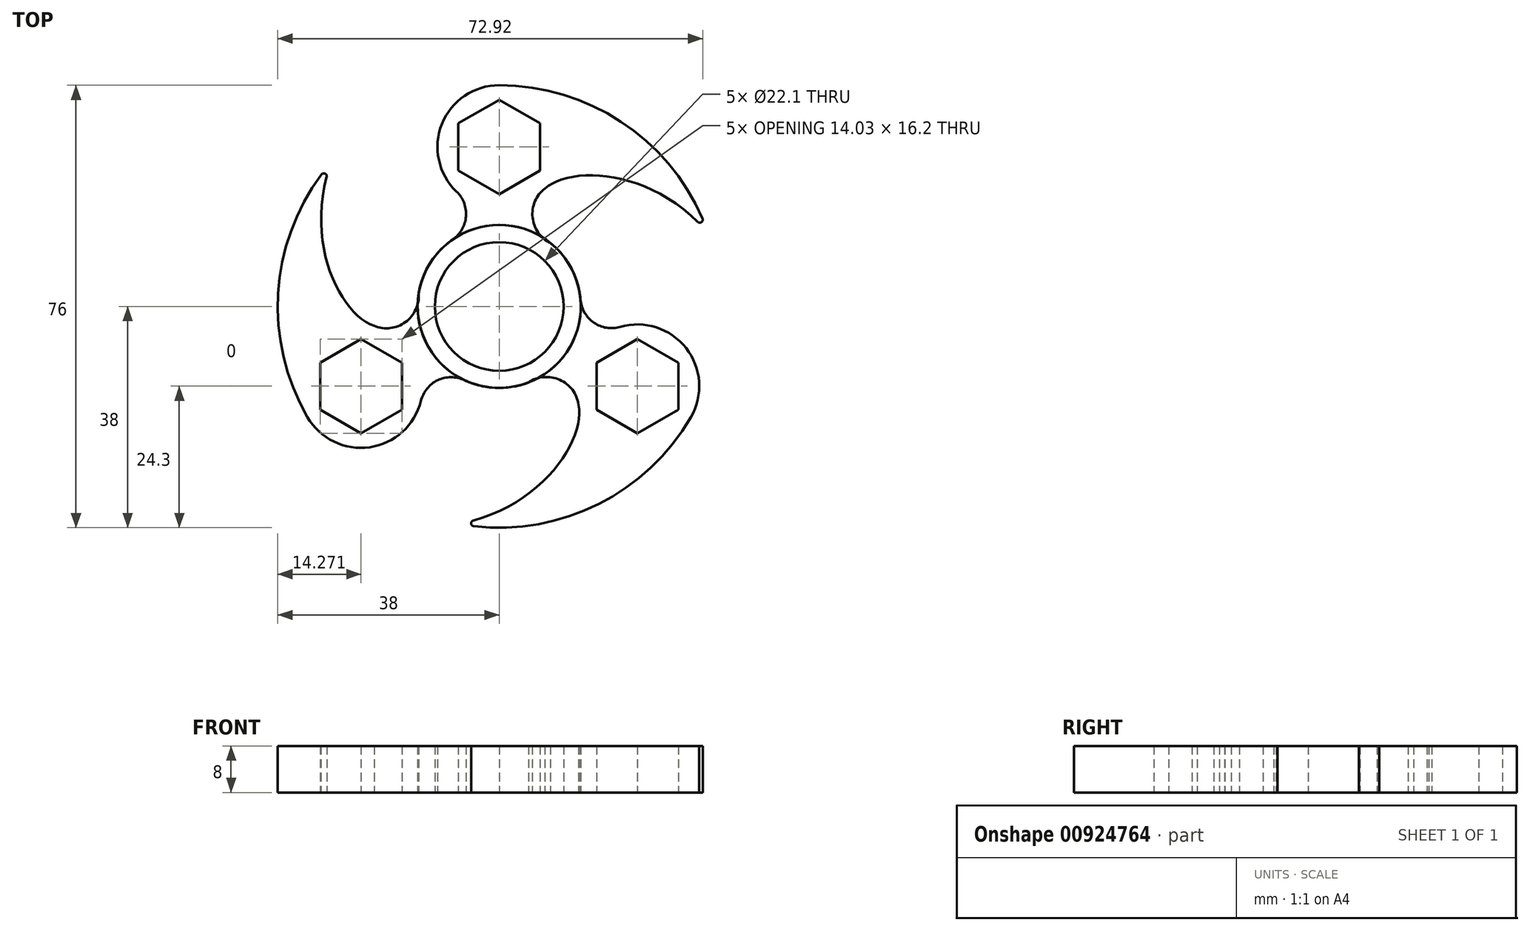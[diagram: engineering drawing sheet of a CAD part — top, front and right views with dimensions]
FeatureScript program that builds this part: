
annotation { "Feature Type Name" : "Feature", "Feature Type Description" : "" }
export const myFeature = defineFeature(function(context is Context, id is Id, definition is map)
    precondition{}
    {
        {
            var Q0;
            Q0=qCreatedBy(makeId("Top.planeOp"),FACE);
            var sketch = newSketch(context, id + "F0", { "sketchPlane" : qUnion([Q0])});
            skCircle(sketch, "E0", {"center": v(0, 0) * mm, "radius": 14 * mm});
            skLineSegment(sketch, "E1", {"start": v(-26.87, 26.87) * mm, "end": v(26.87, -26.87) * mm, "construction": true});
            skLineSegment(sketch, "E2.MirrorCS", {"start": v(26.87, 26.87) * mm, "end": v(-26.87, -26.87) * mm, "construction": true});
            skPoint(sketch, "E3", {"position": v(9.9, -9.9) * mm});
            skPoint(sketch, "E4", {"position": v(-9.9, -9.9) * mm});
            skPoint(sketch, "E5", {"position": v(9.9, 9.9) * mm});
            skPoint(sketch, "E6", {"position": v(-9.9, 9.9) * mm});
            skLineSegment(sketch, "E7", {"start": v(0, 0) * mm, "end": v(-32.9, -19) * mm, "construction": true});
            skLineSegment(sketch, "E8.MirrorCS", {"start": v(0, 0) * mm, "end": v(32.9, -19) * mm, "construction": true});
            skCircle(sketch, "E9.cCircle", {"center": v(23.73, -13.7) * mm, "radius": 7.01 * mm, "construction": true});
            skLineSegment(sketch, "E9.0", {"start": v(16.71, -9.65) * mm, "end": v(23.73, -5.6) * mm});
            skLineSegment(sketch, "E9.1", {"start": v(23.73, -5.6) * mm, "end": v(30.74, -9.65) * mm});
            skLineSegment(sketch, "E9.2", {"start": v(30.74, -9.65) * mm, "end": v(30.74, -17.75) * mm});
            skLineSegment(sketch, "E9.3", {"start": v(30.74, -17.75) * mm, "end": v(23.73, -21.8) * mm});
            skLineSegment(sketch, "E9.4", {"start": v(23.73, -21.8) * mm, "end": v(16.71, -17.75) * mm});
            skLineSegment(sketch, "E9.5", {"start": v(16.71, -17.75) * mm, "end": v(16.71, -9.65) * mm});
            skPoint(sketch, "E9.0.midPoint", {"position": v(20.22, -7.62) * mm});
            skPoint(sketch, "E10", {"position": v(12.12, -7) * mm});
            skPoint(sketch, "E11", {"position": v(12.68, -7.32) * mm});
            skCircle(sketch, "E12", {"center": v(0, 0) * mm, "radius": 38 * mm});
            skCircle(sketch, "E13", {"center": v(23.73, -13.7) * mm, "radius": 10.6 * mm});
            skPoint(sketch, "E14.first.point", {"position": v(13.63, -16.9) * mm});
            skPoint(sketch, "E14.second.point", {"position": v(5.05, -13.06) * mm});
            skPoint(sketch, "E14.third.point", {"position": v(1.3, -17.95) * mm});
            skPoint(sketch, "E15.center", {"position": v(0.94, -0.54) * mm});
            skLineSegment(sketch, "E15.anchor1", {"start": v(0.94, -0.54) * mm, "end": v(23.73, -13.7) * mm, "construction": true});
            skLineSegment(sketch, "E15.anchor2", {"start": v(0.94, -0.54) * mm, "end": v(0.94, 25.78) * mm, "construction": true});
            skFitSpline(sketch, "E16", {"points": [v(13.63, -16.9) * mm, v(-7, -37.35) * mm], "startDerivative": vector(3.53, -17.94) * mm, "endDerivative": vector(-42.9, -7.87) * mm});
            skArc(sketch, "E17", {"start": v(13.63, -16.9) * mm, "mid": v(10.39, -12.6) * mm, "end": v(5.02, -13.07) * mm});
            skArc(sketch, "E18", {"start": v(20.77, -3.52) * mm, "mid": v(16.25, -2.8) * mm, "end": v(13.95, 1.16) * mm});
            skCircle(sketch, "E19", {"center": v(0, 0) * mm, "radius": 11.05 * mm});
            skSolve(sketch);
        }
        {
            var Q0;
            Q0=makeQuery(id+"F0.imprint","IMPRINT",FACE,{"disambiguationData":[TD([[makeQuery(id+"F0.imprint","IMPRINT",EDGE,{"derivedFrom":sQuery(id+"F0.wireOp",EDGE,"E9.0")}),1.0]])]});
            var Q1;
            {var subQ0=sQuery(id+"F0.wireOp",EDGE,"E16");var subQ1=sQuery(id+"F0.wireOp",EDGE,"E12");var subQ2=makeQuery(id+"F0.imprint","INTERSECT",VERTEX,{"derivedFrom":[subQ1,subQ0]});Q1=makeQuery(id+"F0.imprint","IMPRINT",FACE,{"disambiguationData":[TD([[makeQuery(id+"F0.imprint","IMPRINT",EDGE,{"disambiguationData":[TD([[subQ2,-1.0]])],"derivedFrom":subQ1}),1.0]])]});}
            var Q2;
            {var subQ0=sQuery(id+"F0.wireOp",EDGE,"E17");Q2=makeQuery(id+"F0.imprint","IMPRINT",FACE,{"disambiguationData":[TD([[makeQuery(id+"F0.imprint","IMPRINT",EDGE,{"derivedFrom":subQ0}),-1.0]])]});}
            extrude(context, id + "F1", {"entities" : qUnion([Q0, Q1, Q2]), "depth" : 8 * mm, "offsetDistance" : 25 * mm});
        }
        {
            var Q0;
            Q0=qCreatedBy(makeId("Front.planeOp"),FACE);
            var sketch = newSketch(context, id + "F2", { "sketchPlane" : qUnion([Q0])});
            skLineSegment(sketch, "E20", {"start": v(0, 50.96) * mm, "end": v(0, -45.31) * mm, "construction": true});
            skSolve(sketch);
        }
        {
            var Q0;
            Q0=makeQuery(id+"F1.opExtrude","SWEPT_EDGE",EDGE,{"disambiguationData":[OSD([sQuery(id+"F0.wireOp",EDGE,"E12"),sQuery(id+"F0.wireOp",EDGE,"E16")])]});
            fillet(context, id + "F3", {"entities" : qUnion([Q0]), "radius" : .5 * mm, "tangentPropagation" : true, "allowEdgeOverflow" : false});
        }
        {
            var Q0;
            Q0=makeQuery(id+"F1.opExtrude","SWEPT_BODY",BODY,{"disambiguationData":[OSD([sQuery(id+"F0.wireOp",EDGE,"E9.0"),sQuery(id+"F0.wireOp",EDGE,"E9.1"),sQuery(id+"F0.wireOp",EDGE,"E9.2"),sQuery(id+"F0.wireOp",EDGE,"E9.3"),sQuery(id+"F0.wireOp",EDGE,"E9.4"),sQuery(id+"F0.wireOp",EDGE,"E9.5"),sQuery(id+"F0.wireOp",EDGE,"YaXM8q4p-rSk9-f3v4-dJyf-LGJRnrs2c9Lm"),sQuery(id+"F0.wireOp",EDGE,"gtwioz9B-isxs-5wh6-mms0-VsHrY82kivU5"),sQuery(id+"F0.wireOp",EDGE,"51dd48fb-d7a9-4173-a152-bf5a7ab982b3"),sQuery(id+"F0.wireOp",EDGE,"3945e3bb-6025-4d91-b29d-538a82562c9e2")])]});
            var Q1;
            Q1=sQuery(id+"F2.wireOp",EDGE,"E20");
            circularPattern(context, id + "F4", {"entities" : qUnion([Q0]), "axis" : qUnion([Q1]), "angle" : 360 * degree, "instanceCount" : 3, "equalSpace" : true, "isCentered" : true});
        }
    });
